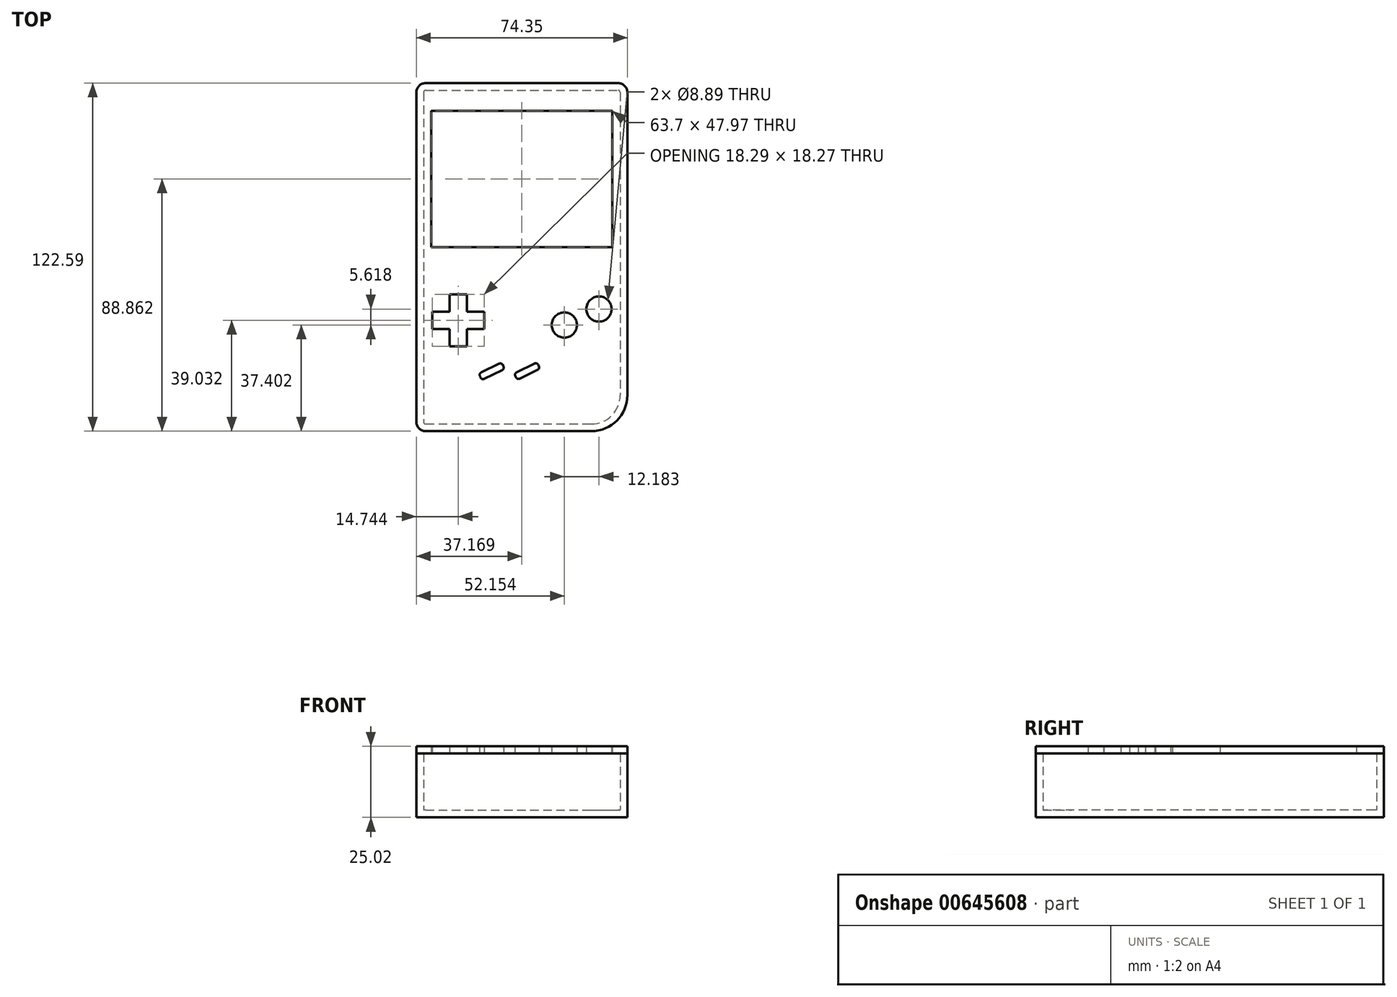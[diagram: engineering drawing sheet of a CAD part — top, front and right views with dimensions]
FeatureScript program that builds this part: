
annotation { "Feature Type Name" : "Feature", "Feature Type Description" : "" }
export const myFeature = defineFeature(function(context is Context, id is Id, definition is map)
    precondition{}
    {
        {
            var Q0;
            Q0=qCreatedBy(makeId("Top.planeOp"),FACE);
            var sketch = newSketch(context, id + "F0", { "sketchPlane" : qUnion([Q0])});
            skLineSegment(sketch, "E0.bottom", {"start": v(-32.81, 69.75) * mm, "end": v(34.93, 69.75) * mm});
            skLineSegment(sketch, "E0.top", {"start": v(-32.81, -52.83) * mm, "end": v(25.53, -52.83) * mm});
            skLineSegment(sketch, "E0.left", {"start": v(-36.11, 66.45) * mm, "end": v(-36.11, -49.53) * mm});
            skLineSegment(sketch, "E0.right", {"start": v(38.23, 66.45) * mm, "end": v(38.23, -40.13) * mm});
            skPoint(sketch, "E1.visualSharp", {"position": v(-36.11, 69.75) * mm});
            skArc(sketch, "E1.filletArc", {"start": v(-32.81, 69.75) * mm, "mid": v(-35.15, 68.78) * mm, "end": v(-36.11, 66.45) * mm});
            skPoint(sketch, "E2.visualSharp", {"position": v(38.23, 69.75) * mm});
            skArc(sketch, "E2.filletArc", {"start": v(38.23, 66.45) * mm, "mid": v(37.26, 68.78) * mm, "end": v(34.93, 69.75) * mm});
            skPoint(sketch, "E3.visualSharp", {"position": v(-36.11, -52.83) * mm});
            skArc(sketch, "E3.filletArc", {"start": v(-36.11, -49.53) * mm, "mid": v(-35.15, -51.86) * mm, "end": v(-32.81, -52.83) * mm});
            skPoint(sketch, "E4.visualSharp", {"position": v(38.23, -52.83) * mm});
            skArc(sketch, "E4.filletArc", {"start": v(25.53, -52.83) * mm, "mid": v(34.51, -49.11) * mm, "end": v(38.23, -40.13) * mm});
            skArc(sketch, "E5.0", {"start": v(-32.81, 67.21) * mm, "mid": v(-33.35, 66.99) * mm, "end": v(-33.57, 66.45) * mm});
            skLineSegment(sketch, "E5.1", {"start": v(-32.81, 67.21) * mm, "end": v(34.93, 67.21) * mm});
            skLineSegment(sketch, "E5.2", {"start": v(-33.57, 66.45) * mm, "end": v(-33.57, -49.53) * mm});
            skArc(sketch, "E5.3", {"start": v(35.7, 66.45) * mm, "mid": v(35.47, 66.99) * mm, "end": v(34.93, 67.21) * mm});
            skArc(sketch, "E5.4", {"start": v(-33.57, -49.53) * mm, "mid": v(-33.35, -50.07) * mm, "end": v(-32.81, -50.3) * mm});
            skLineSegment(sketch, "E5.5", {"start": v(-32.81, -50.3) * mm, "end": v(25.53, -50.3) * mm});
            skArc(sketch, "E5.6", {"start": v(25.53, -50.3) * mm, "mid": v(32.71, -47.32) * mm, "end": v(35.7, -40.13) * mm});
            skLineSegment(sketch, "E5.7", {"start": v(35.7, 66.45) * mm, "end": v(35.7, -40.13) * mm});
            skSolve(sketch);
        }
        {
            var Q0;
            Q0=makeQuery(id+"F0.imprint","IMPRINT",FACE,{"disambiguationData":[TD([[makeQuery(id+"F0.imprint","IMPRINT",EDGE,{"derivedFrom":sQuery(id+"F0.wireOp",EDGE,"E0.bottom")}),-1.0]])]});
            extrude(context, id + "F1", {"entities" : qUnion([Q0]), "depth" : 19.94 * mm, "offsetDistance" : 25.4 * mm});
        }
        {
            var Q0;
            Q0=makeQuery(id+"F1.opExtrude","CAP_FACE",FACE,{"disambiguationData":[OSD([sQuery(id+"F0.wireOp",EDGE,"E0.bottom"),sQuery(id+"F0.wireOp",EDGE,"E0.top"),sQuery(id+"F0.wireOp",EDGE,"E0.left"),sQuery(id+"F0.wireOp",EDGE,"E0.right"),sQuery(id+"F0.wireOp",EDGE,"E1.filletArc"),sQuery(id+"F0.wireOp",EDGE,"E2.filletArc"),sQuery(id+"F0.wireOp",EDGE,"E3.filletArc"),sQuery(id+"F0.wireOp",EDGE,"E4.filletArc")])],"isStart":false});
            var sketch = newSketch(context, id + "F2", { "sketchPlane" : qUnion([Q0])});
            skLineSegment(sketch, "E6.bottom", {"start": v(-30.8, 60) * mm, "end": v(32.9, 60) * mm});
            skLineSegment(sketch, "E6.top", {"start": v(-30.8, 12.04) * mm, "end": v(32.9, 12.04) * mm});
            skLineSegment(sketch, "E6.left", {"start": v(-30.8, 60) * mm, "end": v(-30.8, 12.04) * mm});
            skLineSegment(sketch, "E6.right", {"start": v(32.9, 60) * mm, "end": v(32.9, 12.04) * mm});
            skLineSegment(sketch, "E7.bottom", {"start": v(-24.42, -4.68) * mm, "end": v(-18.33, -4.68) * mm});
            skLineSegment(sketch, "E7.top", {"start": v(-24.42, -22.94) * mm, "end": v(-18.33, -22.94) * mm});
            skLineSegment(sketch, "E7.left", {"start": v(-30.52, -10.75) * mm, "end": v(-30.52, -16.84) * mm});
            skLineSegment(sketch, "E7.right", {"start": v(-12.23, -10.75) * mm, "end": v(-12.23, -16.84) * mm});
            skLineSegment(sketch, "E8", {"start": v(-30.52, -10.75) * mm, "end": v(-24.42, -10.75) * mm});
            skLineSegment(sketch, "E9", {"start": v(-30.52, -16.84) * mm, "end": v(-24.42, -16.84) * mm});
            skLineSegment(sketch, "E10", {"start": v(-24.42, -4.68) * mm, "end": v(-24.42, -10.75) * mm});
            skLineSegment(sketch, "E11", {"start": v(-18.33, -4.68) * mm, "end": v(-18.33, -10.75) * mm});
            skLineSegment(sketch, "E12.trimOffspring", {"start": v(-18.33, -10.75) * mm, "end": v(-12.23, -10.75) * mm});
            skLineSegment(sketch, "E13.trimOffspring", {"start": v(-18.33, -16.84) * mm, "end": v(-18.33, -22.94) * mm});
            skLineSegment(sketch, "E14.trimOffspring", {"start": v(-18.33, -16.84) * mm, "end": v(-12.23, -16.84) * mm});
            skLineSegment(sketch, "E15.trimOffspring", {"start": v(-24.42, -16.84) * mm, "end": v(-24.42, -22.94) * mm});
            skCircle(sketch, "E16", {"center": v(16.03, -15.44) * mm, "radius": 4.45 * mm});
            skCircle(sketch, "E17", {"center": v(28.22, -9.82) * mm, "radius": 4.45 * mm});
            skLineSegment(sketch, "E18", {"start": v(-13.22, -32.13) * mm, "end": v(-6.98, -29.08) * mm});
            skLineSegment(sketch, "E19", {"start": v(-5.62, -29.55) * mm, "end": v(-5.4, -29.98) * mm});
            skLineSegment(sketch, "E20", {"start": v(-5.87, -31.34) * mm, "end": v(-12.14, -34.4) * mm});
            skLineSegment(sketch, "E21", {"start": v(-13.52, -33.89) * mm, "end": v(-13.7, -33.44) * mm});
            skPoint(sketch, "E22.visualSharp", {"position": v(-6.07, -28.63) * mm});
            skArc(sketch, "E22.filletArc", {"start": v(-5.62, -29.55) * mm, "mid": v(-6.2, -29.03) * mm, "end": v(-6.98, -29.08) * mm});
            skPoint(sketch, "E23.visualSharp", {"position": v(-4.96, -30.9) * mm});
            skArc(sketch, "E23.filletArc", {"start": v(-5.87, -31.34) * mm, "mid": v(-5.36, -30.76) * mm, "end": v(-5.4, -29.98) * mm});
            skPoint(sketch, "E24.visualSharp", {"position": v(-13.1, -34.88) * mm});
            skArc(sketch, "E24.filletArc", {"start": v(-13.52, -33.89) * mm, "mid": v(-12.94, -34.44) * mm, "end": v(-12.14, -34.4) * mm});
            skPoint(sketch, "E25.visualSharp", {"position": v(-14.08, -32.55) * mm});
            skArc(sketch, "E25.filletArc", {"start": v(-13.22, -32.13) * mm, "mid": v(-13.72, -32.69) * mm, "end": v(-13.7, -33.44) * mm});
            skPoint(sketch, "E26.visualSharp", {"position": v(-30.8, 12.04) * mm});
            skLineSegment(sketch, "E27", {"start": v(-0.77, -32.06) * mm, "end": v(5.47, -29) * mm});
            skLineSegment(sketch, "E28", {"start": v(6.83, -29.47) * mm, "end": v(7.05, -29.9) * mm});
            skLineSegment(sketch, "E29", {"start": v(6.58, -31.27) * mm, "end": v(0.32, -34.33) * mm});
            skLineSegment(sketch, "E30", {"start": v(-1.06, -33.81) * mm, "end": v(-1.25, -33.36) * mm});
            skPoint(sketch, "E31.visualSharp", {"position": v(6.39, -28.56) * mm});
            skArc(sketch, "E31.filletArc", {"start": v(6.83, -29.47) * mm, "mid": v(6.25, -28.96) * mm, "end": v(5.47, -29) * mm});
            skPoint(sketch, "E32.visualSharp", {"position": v(7.5, -30.82) * mm});
            skArc(sketch, "E32.filletArc", {"start": v(6.58, -31.27) * mm, "mid": v(7.1, -30.68) * mm, "end": v(7.05, -29.9) * mm});
            skPoint(sketch, "E33.visualSharp", {"position": v(-0.65, -34.8) * mm});
            skArc(sketch, "E33.filletArc", {"start": v(-1.06, -33.81) * mm, "mid": v(-0.48, -34.37) * mm, "end": v(0.32, -34.33) * mm});
            skPoint(sketch, "E34.visualSharp", {"position": v(-1.63, -32.48) * mm});
            skArc(sketch, "E34.filletArc", {"start": v(-0.77, -32.06) * mm, "mid": v(-1.27, -32.61) * mm, "end": v(-1.25, -33.36) * mm});
            skSolve(sketch);
        }
        {
            var Q0;
            Q0=makeQuery(id+"F2.imprint","IMPRINT",FACE,{"disambiguationData":[TD([[makeQuery(id+"F2.imprint","IMPRINT",EDGE,{"derivedFrom":sQuery(id+"F2.wireOp",EDGE,"E6.bottom")}),1.0]])]});
            var Q1;
            Q1=makeQuery(id+"F2.imprint","IMPRINT",FACE,{"disambiguationData":[TD([[makeQuery(id+"F2.imprint","IMPRINT",EDGE,{"derivedFrom":makeQuery(id+"F1.opExtrude","CAP_EDGE",EDGE,{"disambiguationData":[OSD([sQuery(id+"F0.wireOp",EDGE,"E0.bottom")])],"isStart":false})}),-1.0]])]});
            extrude(context, id + "F3", {"entities" : qUnion([Q0, Q1]), "depth" : 2.54 * mm, "offsetDistance" : 25.4 * mm});
        }
        {
            var Q0;
            Q0=qCreatedBy(makeId("Top.planeOp"),FACE);
            var sketch = newSketch(context, id + "F4", { "sketchPlane" : qUnion([Q0])});
            skLineSegment(sketch, "E35.bottom", {"start": v(-32.82, 69.74) * mm, "end": v(34.92, 69.74) * mm});
            skLineSegment(sketch, "E35.top", {"start": v(-32.82, -52.84) * mm, "end": v(25.53, -52.84) * mm});
            skLineSegment(sketch, "E35.left", {"start": v(-36.12, 66.44) * mm, "end": v(-36.12, -49.54) * mm});
            skLineSegment(sketch, "E35.right", {"start": v(38.23, 66.44) * mm, "end": v(38.23, -40.14) * mm});
            skPoint(sketch, "E36.visualSharp", {"position": v(-36.12, 69.74) * mm});
            skArc(sketch, "E36.filletArc", {"start": v(-32.82, 69.74) * mm, "mid": v(-35.15, 68.78) * mm, "end": v(-36.12, 66.44) * mm});
            skPoint(sketch, "E37.visualSharp", {"position": v(38.23, 69.74) * mm});
            skArc(sketch, "E37.filletArc", {"start": v(38.23, 66.44) * mm, "mid": v(37.26, 68.78) * mm, "end": v(34.92, 69.74) * mm});
            skPoint(sketch, "E38.visualSharp", {"position": v(-36.12, -52.84) * mm});
            skArc(sketch, "E38.filletArc", {"start": v(-36.12, -49.54) * mm, "mid": v(-35.15, -51.87) * mm, "end": v(-32.82, -52.84) * mm});
            skPoint(sketch, "E39.visualSharp", {"position": v(38.23, -52.84) * mm});
            skArc(sketch, "E39.filletArc", {"start": v(25.53, -52.84) * mm, "mid": v(34.5, -49.12) * mm, "end": v(38.23, -40.14) * mm});
            skSolve(sketch);
        }
        {
            var Q0;
            Q0 = qSketchRegion(id + "F4", true);
            extrude(context, id + "F5", {"entities" : qUnion([Q0]), "operationType" : NewBodyOperationType.ADD, "oppositeDirection" : true, "depth" : 2.54 * mm, "offsetDistance" : 25.4 * mm});
        }
    });
